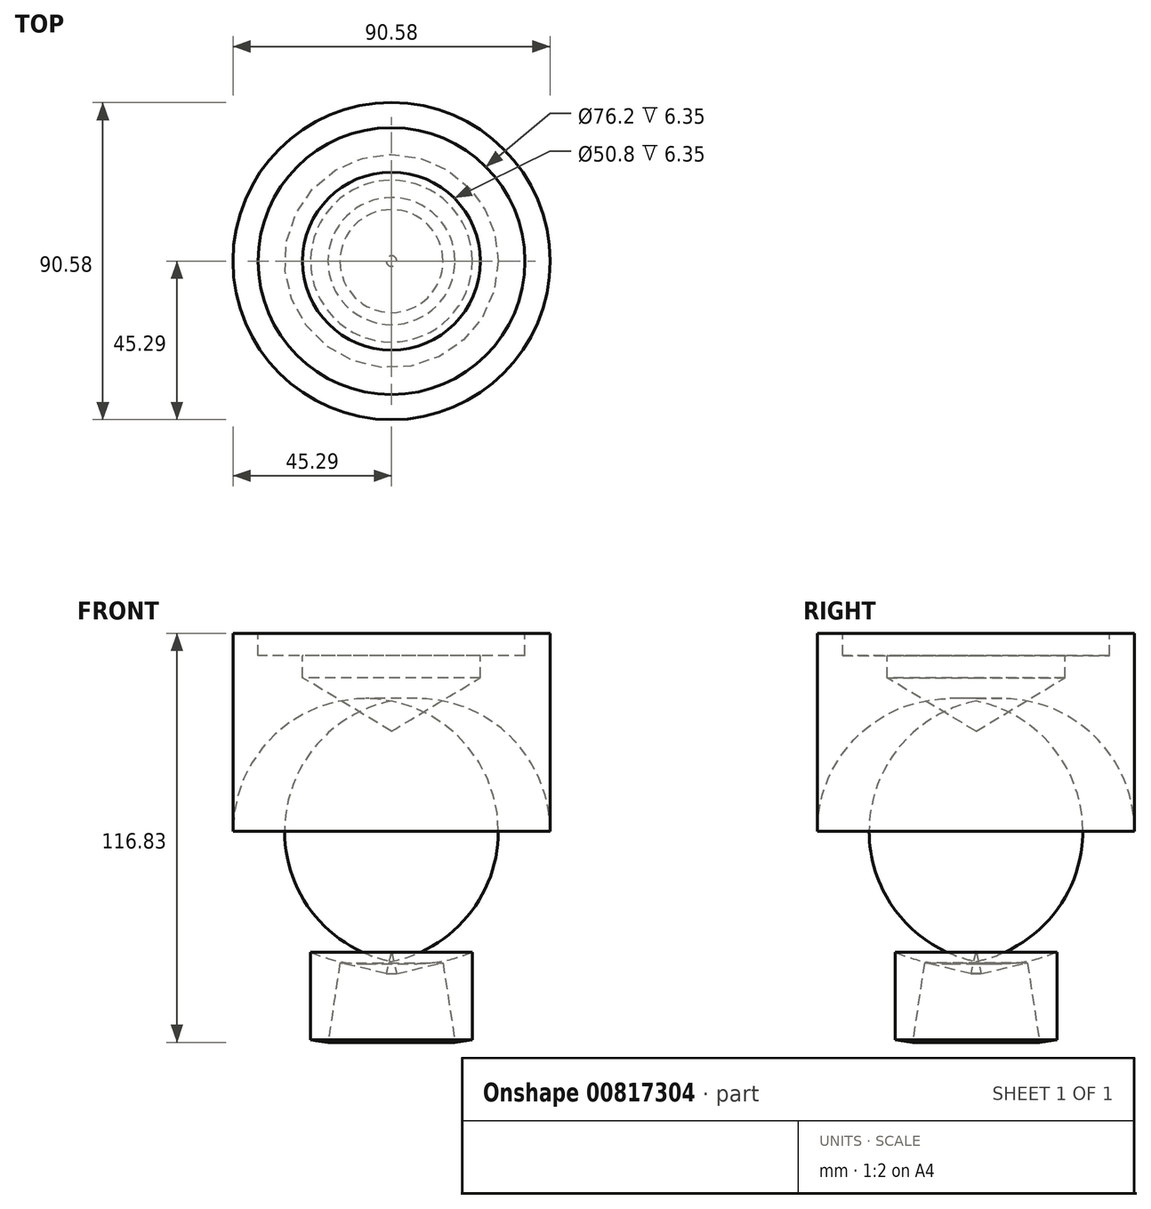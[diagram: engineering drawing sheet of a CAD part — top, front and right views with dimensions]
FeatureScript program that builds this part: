
annotation { "Feature Type Name" : "Feature", "Feature Type Description" : "" }
export const myFeature = defineFeature(function(context is Context, id is Id, definition is map)
    precondition{}
    {
        {
            var Q0;
            Q0=qCreatedBy(makeId("Front.planeOp"),FACE);
            var sketch = newSketch(context, id + "F0", { "sketchPlane" : qUnion([Q0])});
            skLineSegment(sketch, "E0", {"start": v(0, 56.54) * mm, "end": v(45.3, 56.54) * mm});
            skLineSegment(sketch, "E1", {"start": v(45.3, 56.54) * mm, "end": v(45.3, 0) * mm});
            skArc(sketch, "E2", {"start": v(45.3, 0) * mm, "mid": v(39.27, -20.5) * mm, "end": v(23.1, -34.5) * mm});
            skLineSegment(sketch, "E3", {"start": v(23.1, -59.54) * mm, "end": v(23.1, -34.5) * mm});
            skLineSegment(sketch, "E4", {"start": v(23.1, -59.54) * mm, "end": v(18.15, -60.3) * mm});
            skLineSegment(sketch, "E5", {"start": v(18.15, -60.3) * mm, "end": v(14.7, -37.56) * mm});
            skLineSegment(sketch, "E6", {"start": v(14.7, -37.56) * mm, "end": v(1.5, -40.64) * mm});
            skLineSegment(sketch, "E7", {"start": v(1.5, -40.64) * mm, "end": v(0, -34.23) * mm});
            skLineSegment(sketch, "E8", {"start": v(0, -34.23) * mm, "end": v(0, 56.54) * mm});
            skSolve(sketch);
        }
        {
            var Q0;
            Q0=makeQuery(id+"F0.imprint","IMPRINT",FACE,{"disambiguationData":[TD([[makeQuery(id+"F0.imprint","IMPRINT",EDGE,{"derivedFrom":sQuery(id+"F0.wireOp",EDGE,"E0")}),-1.0]])]});
            var Q1;
            Q1=sQuery(id+"F0.wireOp",EDGE,"E8");
            revolve(context, id + "F1", {"surfaceOperationType" : NewSurfaceOperationType.NEW, "entities" : qUnion([Q0]), "axis" : qUnion([Q1]), "revolveType" : RevolveType.FULL});
        }
        {
            var Q0;
            Q0=makeQuery(id+"F1.opRevolve","SWEPT_FACE",FACE,{"disambiguationData":[OSD([sQuery(id+"F0.wireOp",EDGE,"E0")])]});
            var sketch = newSketch(context, id + "F2", { "sketchPlane" : qUnion([Q0])});
            skCircle(sketch, "E9", {"center": v(0, 0) * mm, "radius": 39.68 * mm});
            skSolve(sketch);
        }
        {
            var Q0;
            Q0=sQuery(id+"F2.wireOp",VERTEX,"E9.center");
            var Q1;
            Q1=makeQuery(id+"F1.opRevolve","SWEPT_BODY",BODY,{"disambiguationData":[OSD([sQuery(id+"F0.wireOp",EDGE,"E0"),sQuery(id+"F0.wireOp",EDGE,"E1"),sQuery(id+"F0.wireOp",EDGE,"E2"),sQuery(id+"F0.wireOp",EDGE,"E3"),sQuery(id+"F0.wireOp",EDGE,"E4"),sQuery(id+"F0.wireOp",EDGE,"E5"),sQuery(id+"F0.wireOp",EDGE,"E6"),sQuery(id+"F0.wireOp",EDGE,"E7"),sQuery(id+"F0.wireOp",EDGE,"E8")])]});
            hole(context, id + "F3", {"style" : HoleStyle.C_BORE, "endStyle" : HoleEndStyle.BLIND, "holeDiameter" : 50.8 * mm, "cBoreDiameter" : 76.2 * mm, "cBoreDepth" : 6.35 * mm, "majorDiameter" : 6.35 * mm, "holeDepth" : 12.7 * mm, "isTappedThrough" : true, "tappedDepth" : 12.7 * mm, "tapClearance" : 3, "locations" : qUnion([Q0]), "scope" : qUnion([Q1])});
        }
    });
